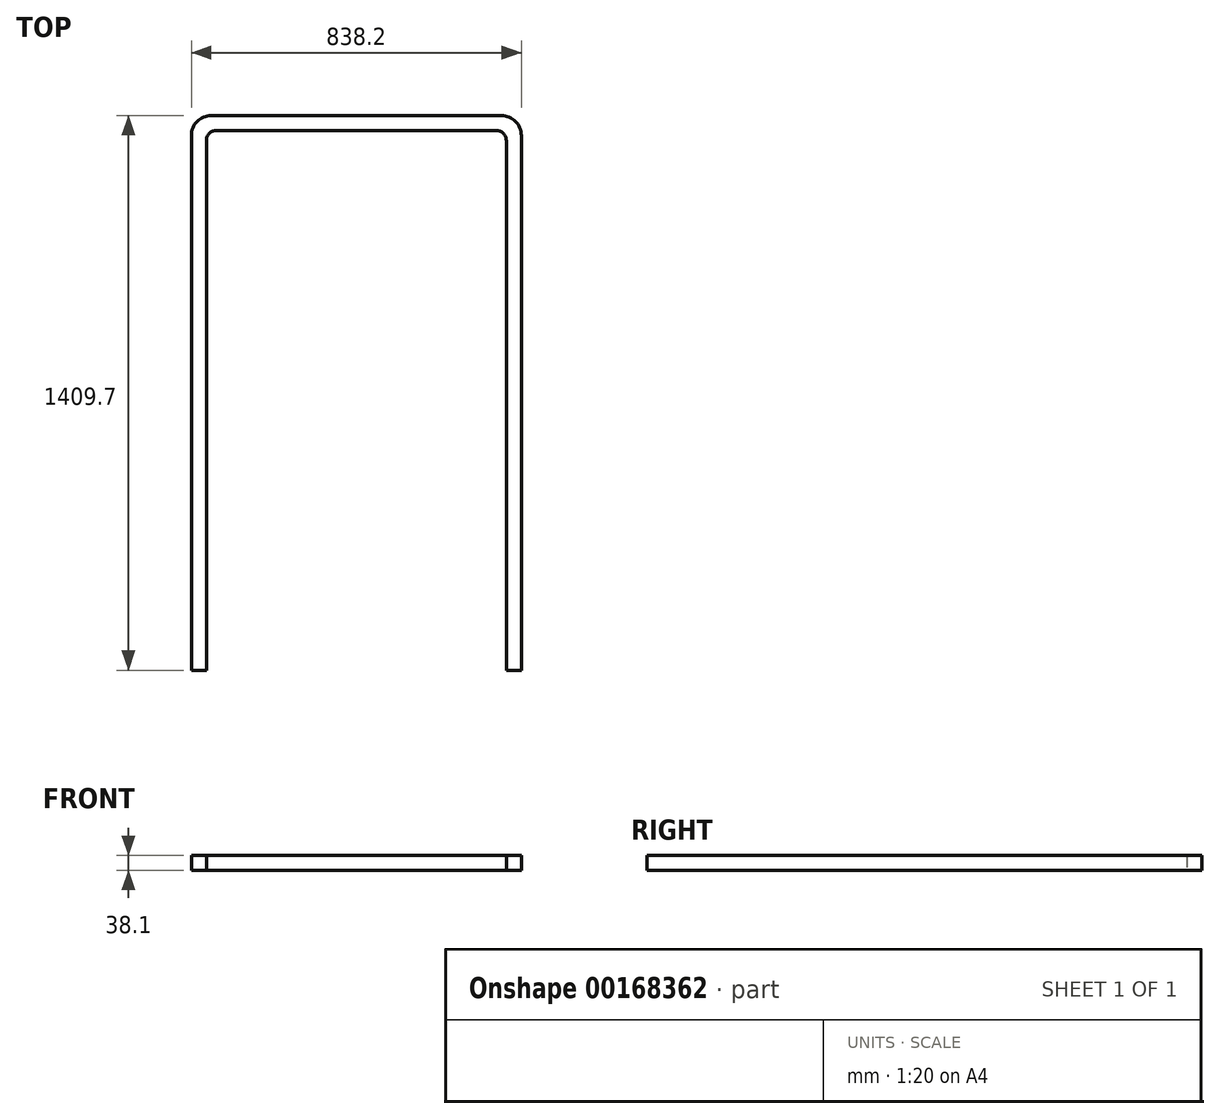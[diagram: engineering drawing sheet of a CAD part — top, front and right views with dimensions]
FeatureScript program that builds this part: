
annotation { "Feature Type Name" : "Feature", "Feature Type Description" : "" }
export const myFeature = defineFeature(function(context is Context, id is Id, definition is map)
    precondition{}
    {
        {
            var Q0;
            Q0=qCreatedBy(makeId("Top.planeOp"),FACE);
            var sketch = newSketch(context, id + "F0", { "sketchPlane" : qUnion([Q0])});
            skLineSegment(sketch, "E0.bottom", {"start": v(-368.3, 704.85) * mm, "end": v(368.3, 704.85) * mm});
            skLineSegment(sketch, "E0.left", {"start": v(-419.1, 654.05) * mm, "end": v(-419.1, -704.85) * mm});
            skLineSegment(sketch, "E0.right", {"start": v(419.1, 654.05) * mm, "end": v(419.1, -704.85) * mm});
            skPoint(sketch, "E0.middle", {"position": v(0, 0) * mm});
            skLineSegment(sketch, "E1.top", {"start": v(-355.6, 666.75) * mm, "end": v(355.6, 666.75) * mm});
            skLineSegment(sketch, "E1.left", {"start": v(-381, -704.85) * mm, "end": v(-381, 641.35) * mm});
            skLineSegment(sketch, "E1.right", {"start": v(381, -704.85) * mm, "end": v(381, 641.35) * mm});
            skLineSegment(sketch, "E2", {"start": v(-419.1, -704.85) * mm, "end": v(-381, -704.85) * mm});
            skLineSegment(sketch, "E3", {"start": v(381, -704.85) * mm, "end": v(419.1, -704.85) * mm});
            skPoint(sketch, "E4.visualSharp", {"position": v(-419.1, 704.85) * mm});
            skArc(sketch, "E4.filletArc", {"start": v(-368.3, 704.85) * mm, "mid": v(-404.22, 689.97) * mm, "end": v(-419.1, 654.05) * mm});
            skPoint(sketch, "E5.visualSharp", {"position": v(-381, 666.75) * mm});
            skArc(sketch, "E5.filletArc", {"start": v(-355.6, 666.75) * mm, "mid": v(-373.56, 659.31) * mm, "end": v(-381, 641.35) * mm});
            skPoint(sketch, "E6.visualSharp", {"position": v(419.1, 704.85) * mm});
            skArc(sketch, "E6.filletArc", {"start": v(419.1, 654.05) * mm, "mid": v(404.22, 689.97) * mm, "end": v(368.3, 704.85) * mm});
            skPoint(sketch, "E7.visualSharp", {"position": v(381, 666.75) * mm});
            skArc(sketch, "E7.filletArc", {"start": v(381, 641.35) * mm, "mid": v(373.56, 659.31) * mm, "end": v(355.6, 666.75) * mm});
            skSolve(sketch);
        }
        {
            var Q0;
            Q0=makeQuery(id+"F0.imprint","IMPRINT",FACE,{"disambiguationData":[TD([[makeQuery(id+"F0.imprint","IMPRINT",EDGE,{"derivedFrom":sQuery(id+"F0.wireOp",EDGE,"E0.bottom")}),-1.0]])]});
            extrude(context, id + "F1", {"entities" : qUnion([Q0]), "depth" : 38.1 * mm});
        }
    });
